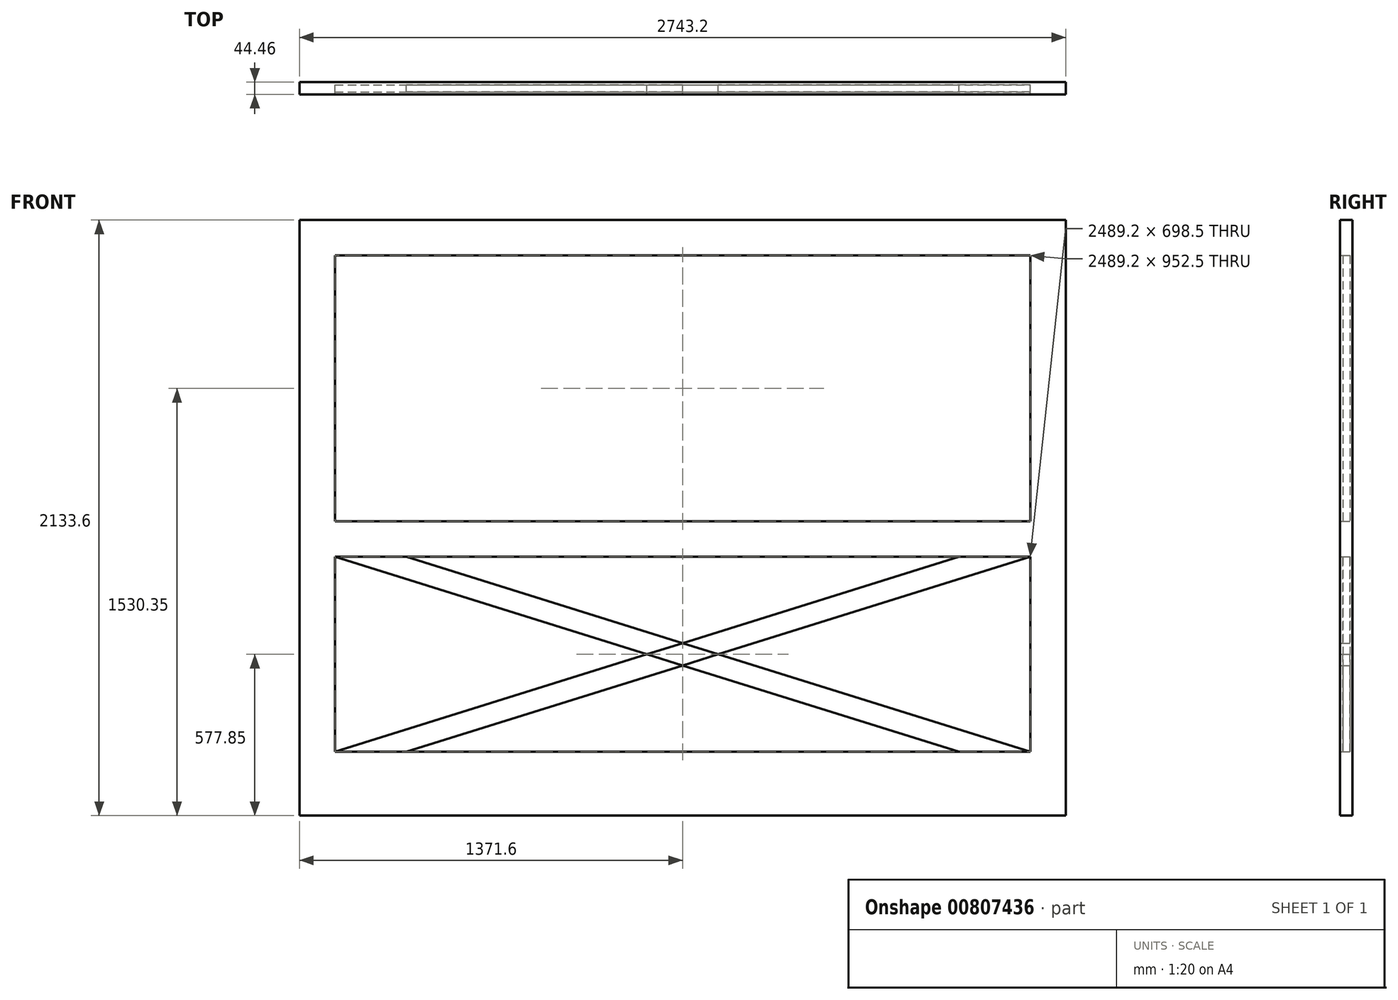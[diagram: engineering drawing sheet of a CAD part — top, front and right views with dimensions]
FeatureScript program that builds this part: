
annotation { "Feature Type Name" : "Feature", "Feature Type Description" : "" }
export const myFeature = defineFeature(function(context is Context, id is Id, definition is map)
    precondition{}
    {
        {
            var Q0;
            Q0=qCreatedBy(makeId("Front.planeOp"),FACE);
            var sketch = newSketch(context, id + "F0", { "sketchPlane" : qUnion([Q0])});
            skLineSegment(sketch, "E0.bottom", {"start": v(-1371.6, 1066.8) * mm, "end": v(1371.6, 1066.8) * mm});
            skLineSegment(sketch, "E0.top", {"start": v(-1371.6, -1066.8) * mm, "end": v(1371.6, -1066.8) * mm});
            skLineSegment(sketch, "E0.left", {"start": v(-1371.6, 1066.8) * mm, "end": v(-1371.6, -1066.8) * mm});
            skLineSegment(sketch, "E0.right", {"start": v(1371.6, 1066.8) * mm, "end": v(1371.6, -1066.8) * mm});
            skPoint(sketch, "E0.middle", {"position": v(0, 0) * mm});
            skLineSegment(sketch, "E1.bottom", {"start": v(-1244.6, 939.8) * mm, "end": v(1244.6, 939.8) * mm});
            skLineSegment(sketch, "E1.top", {"start": v(-1244.6, -838.2) * mm, "end": v(1244.6, -838.2) * mm});
            skLineSegment(sketch, "E1.left", {"start": v(-1244.6, 939.8) * mm, "end": v(-1244.6, -838.2) * mm});
            skLineSegment(sketch, "E1.right", {"start": v(1244.6, 939.8) * mm, "end": v(1244.6, -838.2) * mm});
            skPoint(sketch, "E1.middle", {"position": v(0, 50.8) * mm});
            skLineSegment(sketch, "E2.bottom", {"start": v(-1244.6, -12.7) * mm, "end": v(1244.6, -12.7) * mm});
            skLineSegment(sketch, "E2.top", {"start": v(-1244.6, -139.7) * mm, "end": v(1244.6, -139.7) * mm});
            skLineSegment(sketch, "E2.left", {"start": v(-1244.6, -12.7) * mm, "end": v(-1244.6, -139.7) * mm});
            skLineSegment(sketch, "E2.right", {"start": v(1244.6, -12.7) * mm, "end": v(1244.6, -139.7) * mm});
            skLineSegment(sketch, "E3", {"start": v(-1244.6, -139.7) * mm, "end": v(989.27, -838.2) * mm});
            skLineSegment(sketch, "E4", {"start": v(989.27, -838.2) * mm, "end": v(1244.6, -838.2) * mm});
            skLineSegment(sketch, "E5", {"start": v(1244.6, -838.2) * mm, "end": v(-989.27, -139.7) * mm});
            skLineSegment(sketch, "E6", {"start": v(-989.27, -139.7) * mm, "end": v(-1244.6, -139.7) * mm});
            skLineSegment(sketch, "E7", {"start": v(-1244.6, -838.2) * mm, "end": v(989.27, -139.7) * mm});
            skLineSegment(sketch, "E8", {"start": v(989.27, -139.7) * mm, "end": v(1244.6, -139.7) * mm});
            skLineSegment(sketch, "E9", {"start": v(1244.6, -139.7) * mm, "end": v(-989.27, -838.2) * mm});
            skLineSegment(sketch, "E10", {"start": v(-989.27, -838.2) * mm, "end": v(-1244.6, -838.2) * mm});
            skSolve(sketch);
        }
        {
            var Q0;
            Q0 = qSketchRegion(id + "F0", true);
            var Q1;
            Q1=makeQuery(id+"F0.imprint","IMPRINT",FACE,{"disambiguationData":[TD([[makeQuery(id+"F0.imprint","IMPRINT",EDGE,{"derivedFrom":sQuery(id+"F0.wireOp",EDGE,"E2.bottom")}),-1.0]])]});
            var Q2;
            {var subQ5=sQuery(id+"F0.wireOp",EDGE,"E8");Q2=makeQuery(id+"F0.imprint","IMPRINT",FACE,{"disambiguationData":[TD([[makeQuery(id+"F0.imprint","IMPRINT",EDGE,{"derivedFrom":subQ5}),-1.0]])]});}
            var Q3;
            {var subQ0=sQuery(id+"F0.wireOp",EDGE,"E7");var subQ1=sQuery(id+"F0.wireOp",EDGE,"E3");var subQ2=makeQuery(id+"F0.imprint","INTERSECT",VERTEX,{"derivedFrom":[subQ1,subQ0]});Q3=makeQuery(id+"F0.imprint","IMPRINT",FACE,{"disambiguationData":[TD([[makeQuery(id+"F0.imprint","IMPRINT",EDGE,{"disambiguationData":[TD([[subQ2,-1.0]])],"derivedFrom":subQ1}),1.0]])]});}
            var Q4;
            {var subQ0=sQuery(id+"F0.wireOp",EDGE,"E6");Q4=makeQuery(id+"F0.imprint","IMPRINT",FACE,{"disambiguationData":[TD([[makeQuery(id+"F0.imprint","IMPRINT",EDGE,{"derivedFrom":subQ0}),1.0]])]});}
            var Q5;
            {var subQ0=sQuery(id+"F0.wireOp",EDGE,"E4");Q5=makeQuery(id+"F0.imprint","IMPRINT",FACE,{"disambiguationData":[TD([[makeQuery(id+"F0.imprint","IMPRINT",EDGE,{"derivedFrom":subQ0}),1.0]])]});}
            var Q6;
            {var subQ5=sQuery(id+"F0.wireOp",EDGE,"E10");Q6=makeQuery(id+"F0.imprint","IMPRINT",FACE,{"disambiguationData":[TD([[makeQuery(id+"F0.imprint","IMPRINT",EDGE,{"derivedFrom":subQ5}),-1.0]])]});}
            extrude(context, id + "F1", {"entities" : qUnion([Q0, Q1, Q2, Q3, Q4, Q5, Q6]), "endBound" : BoundingType.SYMMETRIC, "depth" : 44.45 * mm, "offsetDistance" : 25.4 * mm});
        }
        {
            var Q0;
            {var subQ0=sQuery(id+"F0.wireOp",EDGE,"E1.bottom");Q0=makeQuery(id+"F0.imprint","IMPRINT",FACE,{"disambiguationData":[TD([[makeQuery(id+"F0.imprint","IMPRINT",EDGE,{"derivedFrom":subQ0}),-1.0]])]});}
            var Q1;
            {var subQ0=sQuery(id+"F0.wireOp",EDGE,"E2.top");Q1=makeQuery(id+"F0.imprint","IMPRINT",FACE,{"disambiguationData":[TD([[makeQuery(id+"F0.imprint","IMPRINT",EDGE,{"derivedFrom":subQ0}),-1.0]])]});}
            var Q2;
            {var subQ0=sQuery(id+"F0.wireOp",EDGE,"E5");var subQ3=sQuery(id+"F0.wireOp",EDGE,"E9");var subQ5=makeQuery(id+"F0.imprint","INTERSECT",VERTEX,{"derivedFrom":[subQ0,subQ3]});Q2=makeQuery(id+"F0.imprint","IMPRINT",FACE,{"disambiguationData":[TD([[makeQuery(id+"F0.imprint","IMPRINT",EDGE,{"disambiguationData":[TD([[subQ5,1.0]])],"derivedFrom":subQ0}),-1.0]])]});}
            var Q3;
            {var subQ0=sQuery(id+"F0.wireOp",EDGE,"E1.top");Q3=makeQuery(id+"F0.imprint","IMPRINT",FACE,{"disambiguationData":[TD([[makeQuery(id+"F0.imprint","IMPRINT",EDGE,{"derivedFrom":subQ0}),1.0]])]});}
            var Q4;
            {var subQ0=sQuery(id+"F0.wireOp",EDGE,"E7");var subQ3=sQuery(id+"F0.wireOp",EDGE,"E3");var subQ5=makeQuery(id+"F0.imprint","INTERSECT",VERTEX,{"derivedFrom":[subQ3,subQ0]});Q4=makeQuery(id+"F0.imprint","IMPRINT",FACE,{"disambiguationData":[TD([[makeQuery(id+"F0.imprint","IMPRINT",EDGE,{"disambiguationData":[TD([[subQ5,1.0]])],"derivedFrom":subQ0}),1.0]])]});}
            extrude(context, id + "F2", {"entities" : qUnion([Q0, Q1, Q2, Q3, Q4]), "endBound" : BoundingType.SYMMETRIC, "depth" : 25.4 * mm, "offsetDistance" : 25.4 * mm});
        }
    });
